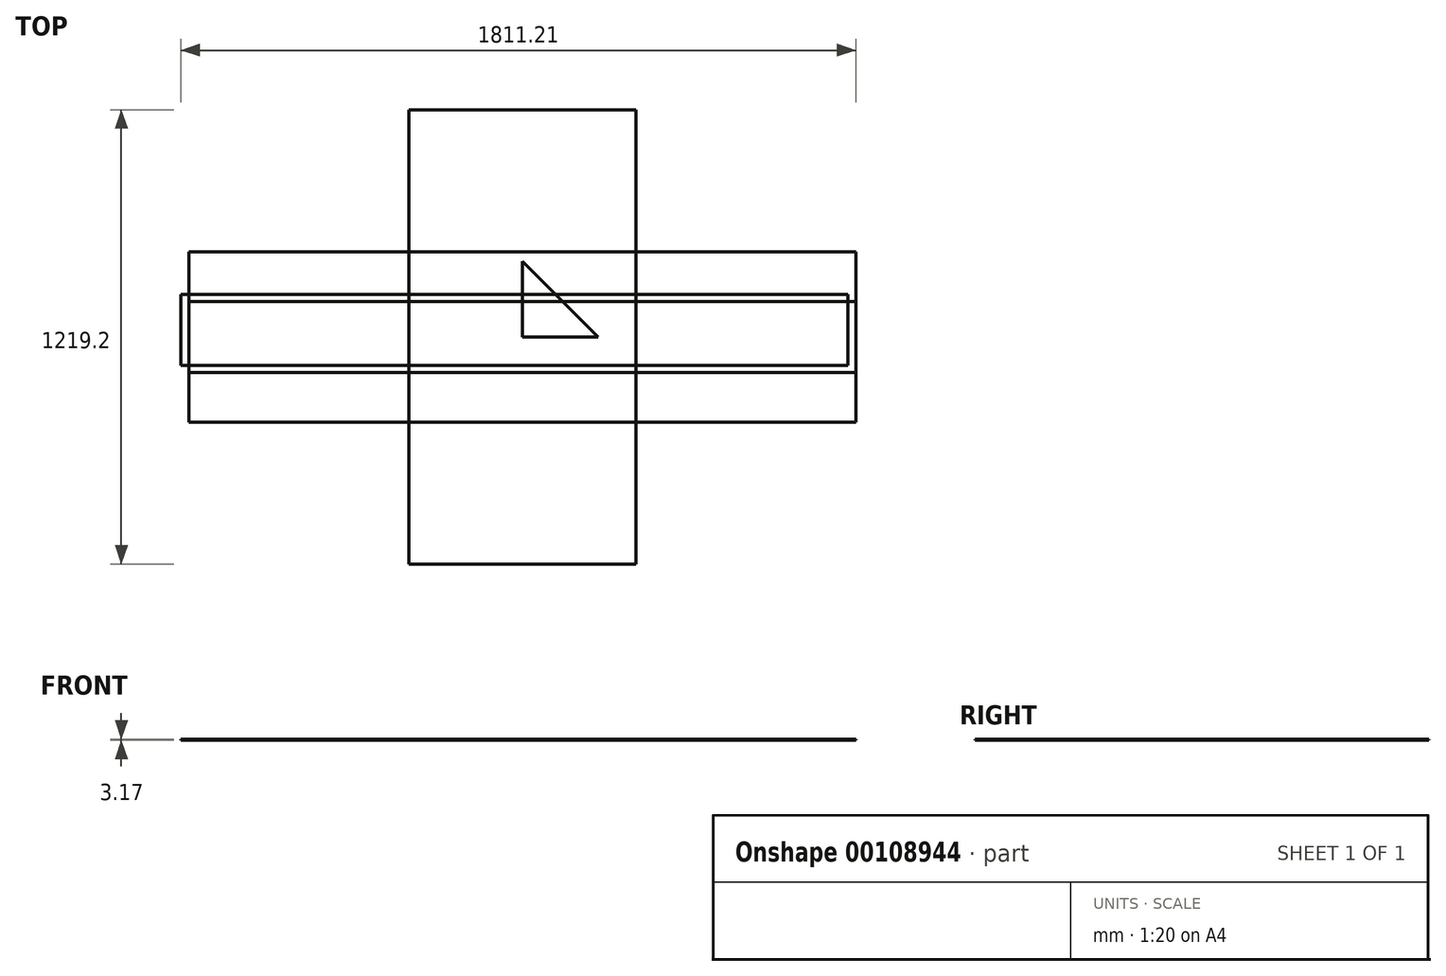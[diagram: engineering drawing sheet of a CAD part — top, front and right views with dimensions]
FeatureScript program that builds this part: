
annotation { "Feature Type Name" : "Feature", "Feature Type Description" : "" }
export const myFeature = defineFeature(function(context is Context, id is Id, definition is map)
    precondition{}
    {
        {
            var Q0;
            Q0=qCreatedBy(makeId("Top.planeOp"),FACE);
            var sketch = newSketch(context, id + "F0", { "sketchPlane" : qUnion([Q0])});
            skLineSegment(sketch, "E0.bottom", {"start": v(-895.35, -95.25) * mm, "end": v(895.35, -95.25) * mm});
            skLineSegment(sketch, "E0.top", {"start": v(-895.35, 95.25) * mm, "end": v(895.35, 95.25) * mm});
            skLineSegment(sketch, "E0.left", {"start": v(-895.35, -95.25) * mm, "end": v(-895.35, 95.25) * mm});
            skLineSegment(sketch, "E0.right", {"start": v(895.35, -95.25) * mm, "end": v(895.35, 95.25) * mm});
            skPoint(sketch, "E0.middle", {"position": v(0, 0) * mm});
            skPoint(sketch, "E1", {"position": v(-806.45, 95.25) * mm});
            skPoint(sketch, "E2", {"position": v(-806.45, -95.25) * mm});
            skPoint(sketch, "E3", {"position": v(806.45, 95.25) * mm});
            skPoint(sketch, "E4", {"position": v(806.45, -95.25) * mm});
            skLineSegment(sketch, "E5.bottom", {"start": v(-806.45, -95.25) * mm, "end": v(806.45, -95.25) * mm});
            skLineSegment(sketch, "E5.top", {"start": v(-806.45, -152.4) * mm, "end": v(806.45, -152.4) * mm});
            skLineSegment(sketch, "E5.left", {"start": v(-806.45, -95.25) * mm, "end": v(-806.45, -152.4) * mm});
            skLineSegment(sketch, "E5.right", {"start": v(806.45, -95.25) * mm, "end": v(806.45, -152.4) * mm});
            skLineSegment(sketch, "E6.bottom", {"start": v(806.45, 95.25) * mm, "end": v(-806.45, 95.25) * mm});
            skLineSegment(sketch, "E6.top", {"start": v(806.45, 152.4) * mm, "end": v(-806.45, 152.4) * mm});
            skLineSegment(sketch, "E6.left", {"start": v(806.45, 95.25) * mm, "end": v(806.45, 152.4) * mm});
            skLineSegment(sketch, "E6.right", {"start": v(-806.45, 95.25) * mm, "end": v(-806.45, 152.4) * mm});
            skSolve(sketch);
        }
        {
            var Q0;
            {var subQ3=sQuery(id+"F0.wireOp",EDGE,"E0.left");Q0=makeQuery(id+"F0.imprint","IMPRINT",FACE,{"disambiguationData":[TD([[makeQuery(id+"F0.imprint","IMPRINT",EDGE,{"derivedFrom":subQ3}),-1.0]])]});}
            var Q1;
            Q1=makeQuery(id+"F0.imprint","IMPRINT",FACE,{"disambiguationData":[TD([[makeQuery(id+"F0.imprint","IMPRINT",EDGE,{"derivedFrom":sQuery(id+"F0.wireOp",EDGE,"E6.bottom")}),-1.0]])]});
            var Q2;
            Q2=makeQuery(id+"F0.imprint","IMPRINT",FACE,{"disambiguationData":[TD([[makeQuery(id+"F0.imprint","IMPRINT",EDGE,{"derivedFrom":sQuery(id+"F0.wireOp",EDGE,"E5.bottom")}),-1.0]])]});
            extrude(context, id + "F1", {"entities" : qUnion([Q0, Q1, Q2]), "depth" : 3.17 * mm});
        }
        {
            var Q0;
            Q0=qCreatedBy(makeId("Top.planeOp"),FACE);
            var sketch = newSketch(context, id + "F2", { "sketchPlane" : qUnion([Q0])});
            skLineSegment(sketch, "E7.bottom", {"start": v(-915.86, -77.3) * mm, "end": v(874.84, -77.3) * mm});
            skLineSegment(sketch, "E7.top", {"start": v(-915.86, 113.2) * mm, "end": v(874.84, 113.2) * mm});
            skLineSegment(sketch, "E7.left", {"start": v(-915.86, -77.3) * mm, "end": v(-915.86, 113.2) * mm});
            skLineSegment(sketch, "E7.right", {"start": v(874.84, -77.3) * mm, "end": v(874.84, 113.2) * mm});
            skPoint(sketch, "E7.middle", {"position": v(-20.51, 17.95) * mm});
            skPoint(sketch, "E8", {"position": v(-826.96, 113.2) * mm});
            skPoint(sketch, "E9", {"position": v(-826.96, -77.3) * mm});
            skPoint(sketch, "E10", {"position": v(785.94, 113.2) * mm});
            skPoint(sketch, "E11", {"position": v(785.94, -77.3) * mm});
            skLineSegment(sketch, "E12.bottom", {"start": v(-826.96, -77.3) * mm, "end": v(785.94, -77.3) * mm});
            skLineSegment(sketch, "E12.top", {"start": v(-826.96, -115.4) * mm, "end": v(785.94, -115.4) * mm});
            skLineSegment(sketch, "E12.left", {"start": v(-826.96, -77.3) * mm, "end": v(-826.96, -115.4) * mm});
            skLineSegment(sketch, "E12.right", {"start": v(785.94, -77.3) * mm, "end": v(785.94, -115.4) * mm});
            skLineSegment(sketch, "E13.bottom", {"start": v(785.94, 113.2) * mm, "end": v(-826.96, 113.2) * mm});
            skLineSegment(sketch, "E13.top", {"start": v(785.94, 151.3) * mm, "end": v(-826.96, 151.3) * mm});
            skLineSegment(sketch, "E13.left", {"start": v(785.94, 113.2) * mm, "end": v(785.94, 151.3) * mm});
            skLineSegment(sketch, "E13.right", {"start": v(-826.96, 113.2) * mm, "end": v(-826.96, 151.3) * mm});
            skSolve(sketch);
        }
        {
            var Q0;
            {var subQ3=sQuery(id+"F2.wireOp",EDGE,"E7.left");Q0=makeQuery(id+"F2.imprint","IMPRINT",FACE,{"disambiguationData":[TD([[makeQuery(id+"F2.imprint","IMPRINT",EDGE,{"derivedFrom":subQ3}),-1.0]])]});}
            var Q1;
            Q1=makeQuery(id+"F2.imprint","IMPRINT",FACE,{"disambiguationData":[TD([[makeQuery(id+"F2.imprint","IMPRINT",EDGE,{"derivedFrom":sQuery(id+"F2.wireOp",EDGE,"E13.bottom")}),-1.0]])]});
            var Q2;
            Q2=makeQuery(id+"F2.imprint","IMPRINT",FACE,{"disambiguationData":[TD([[makeQuery(id+"F2.imprint","IMPRINT",EDGE,{"derivedFrom":sQuery(id+"F2.wireOp",EDGE,"E12.bottom")}),-1.0]])]});
            extrude(context, id + "F3", {"entities" : qUnion([Q0, Q1, Q2]), "depth" : 3.17 * mm});
        }
        {
            var Q0;
            Q0=qCreatedBy(makeId("Top.planeOp"),FACE);
            var sketch = newSketch(context, id + "F4", { "sketchPlane" : qUnion([Q0])});
            skLineSegment(sketch, "E14.bottom", {"start": v(895.35, -228.6) * mm, "end": v(-895.35, -228.6) * mm});
            skLineSegment(sketch, "E14.top", {"start": v(895.35, 228.6) * mm, "end": v(-895.35, 228.6) * mm});
            skLineSegment(sketch, "E14.left", {"start": v(895.35, -228.6) * mm, "end": v(895.35, 228.6) * mm});
            skLineSegment(sketch, "E14.right", {"start": v(-895.35, -228.6) * mm, "end": v(-895.35, 228.6) * mm});
            skPoint(sketch, "E14.middle", {"position": v(0, 0) * mm});
            skSolve(sketch);
        }
        {
            var Q0;
            Q0=makeQuery(id+"F4.imprint","IMPRINT",FACE,{"disambiguationData":[TD([[makeQuery(id+"F4.imprint","IMPRINT",EDGE,{"derivedFrom":sQuery(id+"F4.wireOp",EDGE,"E14.bottom")}),-1.0]])]});
            extrude(context, id + "F5", {"entities" : qUnion([Q0]), "depth" : 3.17 * mm});
        }
        {
            var Q0;
            Q0=qCreatedBy(makeId("Top.planeOp"),FACE);
            var sketch = newSketch(context, id + "F6", { "sketchPlane" : qUnion([Q0])});
            skLineSegment(sketch, "E15.bottom", {"start": v(0, 0) * mm, "end": v(203.2, 0) * mm});
            skLineSegment(sketch, "E15.left", {"start": v(0, 0) * mm, "end": v(0, 203.2) * mm});
            skLineSegment(sketch, "E16", {"start": v(0, 203.2) * mm, "end": v(203.2, 0) * mm});
            skSolve(sketch);
        }
        {
            var Q0;
            Q0=makeQuery(id+"F6.imprint","IMPRINT",FACE,{"disambiguationData":[TD([[makeQuery(id+"F6.imprint","IMPRINT",EDGE,{"derivedFrom":sQuery(id+"F6.wireOp",EDGE,"E15.bottom")}),1.0]])]});
            extrude(context, id + "F7", {"entities" : qUnion([Q0]), "depth" : 3.17 * mm});
        }
        {
            var Q0;
            Q0=qCreatedBy(makeId("Top.planeOp"),FACE);
            var sketch = newSketch(context, id + "F8", { "sketchPlane" : qUnion([Q0])});
            skLineSegment(sketch, "E17.bottom", {"start": v(304.8, 609.6) * mm, "end": v(-304.8, 609.6) * mm});
            skLineSegment(sketch, "E17.top", {"start": v(304.8, -609.6) * mm, "end": v(-304.8, -609.6) * mm});
            skLineSegment(sketch, "E17.left", {"start": v(304.8, 609.6) * mm, "end": v(304.8, -609.6) * mm});
            skLineSegment(sketch, "E17.right", {"start": v(-304.8, 609.6) * mm, "end": v(-304.8, -609.6) * mm});
            skPoint(sketch, "E17.middle", {"position": v(0, 0) * mm});
            skSolve(sketch);
        }
        {
            var Q0;
            Q0=makeQuery(id+"F8.imprint","IMPRINT",FACE,{"disambiguationData":[TD([[makeQuery(id+"F8.imprint","IMPRINT",EDGE,{"derivedFrom":sQuery(id+"F8.wireOp",EDGE,"E17.bottom")}),1.0]])]});
            extrude(context, id + "F9", {"entities" : qUnion([Q0]), "depth" : 3.17 * mm});
        }
    });
